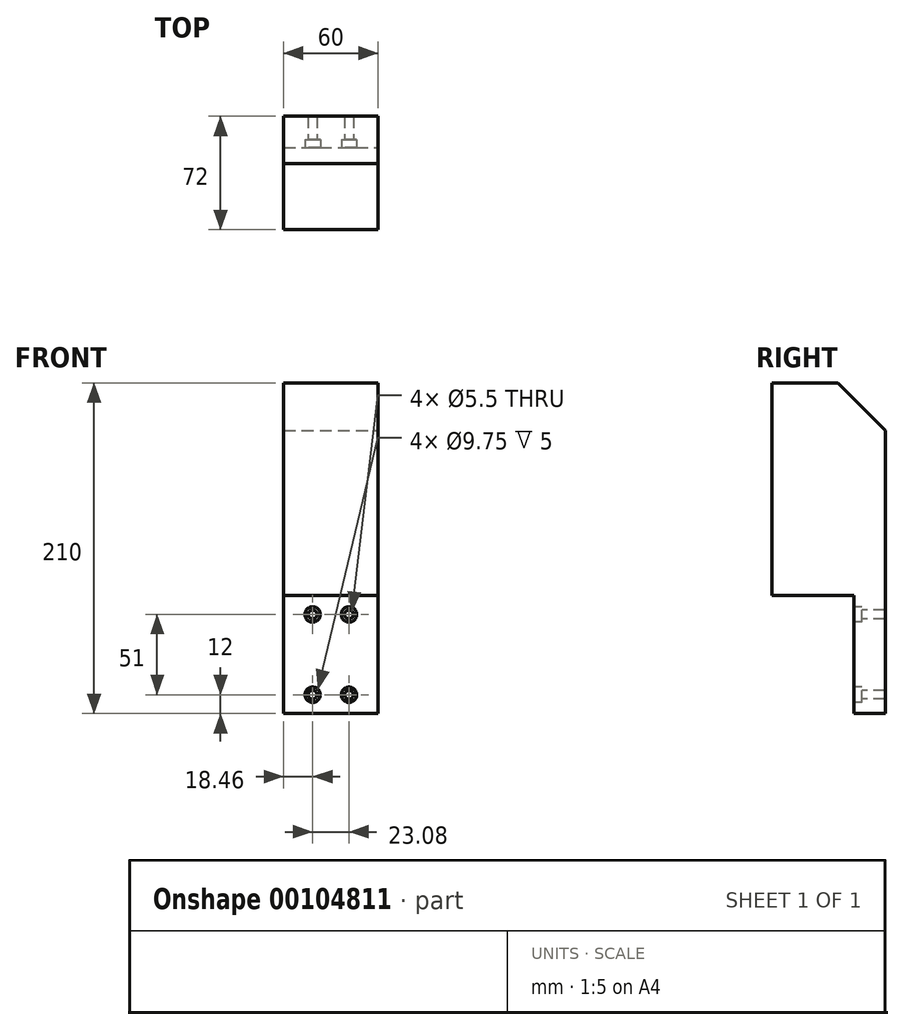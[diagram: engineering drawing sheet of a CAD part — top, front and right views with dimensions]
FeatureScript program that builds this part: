
annotation { "Feature Type Name" : "Feature", "Feature Type Description" : "" }
export const myFeature = defineFeature(function(context is Context, id is Id, definition is map)
    precondition{}
    {
        {
            var Q0;
            Q0=qCreatedBy(makeId("Front.planeOp"),FACE);
            var sketch = newSketch(context, id + "F0", { "sketchPlane" : qUnion([Q0])});
            skLineSegment(sketch, "E0.bottom", {"start": v(-30, 105) * mm, "end": v(30, 105) * mm});
            skLineSegment(sketch, "E0.top", {"start": v(-30, -105) * mm, "end": v(30, -105) * mm});
            skLineSegment(sketch, "E0.left", {"start": v(-30, 105) * mm, "end": v(-30, -105) * mm});
            skLineSegment(sketch, "E0.right", {"start": v(30, 105) * mm, "end": v(30, -105) * mm});
            skPoint(sketch, "E0.middle", {"position": v(0, 0) * mm});
            skSolve(sketch);
        }
        {
            var Q0;
            Q0 = qSketchRegion(id + "F0", true);
            extrude(context, id + "F1", {"entities" : qUnion([Q0]), "depth" : 72 * mm});
        }
        {
            var Q0;
            Q0=makeQuery(id+"F1.opExtrude","SWEPT_FACE",FACE,{"disambiguationData":[OSD([sQuery(id+"F0.wireOp",EDGE,"E0.right")])]});
            var sketch = newSketch(context, id + "F2", { "sketchPlane" : qUnion([Q0])});
            skLineSegment(sketch, "E1.bottom", {"start": v(-72, -105) * mm, "end": v(-20, -105) * mm});
            skLineSegment(sketch, "E1.top", {"start": v(-72, -30) * mm, "end": v(-20, -30) * mm});
            skLineSegment(sketch, "E1.left", {"start": v(-72, -105) * mm, "end": v(-72, -30) * mm});
            skLineSegment(sketch, "E1.right", {"start": v(-20, -105) * mm, "end": v(-20, -30) * mm});
            skSolve(sketch);
        }
        {
            var Q0;
            Q0 = qSketchRegion(id + "F2", true);
            extrude(context, id + "F3", {"entities" : qUnion([Q0]), "operationType" : NewBodyOperationType.REMOVE, "endBound" : BoundingType.THROUGH_ALL, "oppositeDirection" : true, "depth" : 25.4 * mm});
        }
        {
            var Q0;
            Q0=makeQuery(id+"F1.opExtrude","CAP_EDGE",EDGE,{"disambiguationData":[OSD([sQuery(id+"F0.wireOp",EDGE,"E0.bottom")])],"isStart":true});
            chamfer(context, id + "F4", {"entities" : qUnion([Q0]), "width" : 30 * mm, "tangentPropagation" : true});
        }
        {
            var Q0;
            Q0=makeQuery(id+"F3.boolean.opBoolean","COPY",FACE,{"derivedFrom":makeQuery(id+"F3.opExtrude","SWEPT_FACE",FACE,{"disambiguationData":[OSD([sQuery(id+"F2.wireOp",EDGE,"E1.right")])]})});
            cPlane(context, id + "F5", {"entities" : qUnion([Q0]), "cplaneType" : CPlaneType.OFFSET, "offset" : 0 * mm, "width" : 152.4 * mm, "height" : 152.4 * mm});
        }
        {
            var Q0;
            Q0=qCreatedBy(id+"F5.planeOp",FACE);
            var sketch = newSketch(context, id + "F6", { "sketchPlane" : qUnion([Q0])});
            skPoint(sketch, "E2", {"position": v(-11.54, -42) * mm});
            skPoint(sketch, "E3", {"position": v(11.54, -42) * mm});
            skPoint(sketch, "E4", {"position": v(-11.54, -93) * mm});
            skPoint(sketch, "E5", {"position": v(11.54, -93) * mm});
            skLineSegment(sketch, "E6", {"start": v(0, -19.47) * mm, "end": v(0, -135.95) * mm});
            skSolve(sketch);
        }
        {
            var Q0;
            Q0=sQuery(id+"F6.wireOp",VERTEX,"E2");
            var Q1;
            Q1=sQuery(id+"F6.wireOp",VERTEX,"E3");
            var Q2;
            Q2=sQuery(id+"F6.wireOp",VERTEX,"E4");
            var Q3;
            Q3=sQuery(id+"F6.wireOp",VERTEX,"E5");
            var Q4;
            Q4=makeQuery(id+"F1.opExtrude","SWEPT_BODY",BODY,{"disambiguationData":[OSD([sQuery(id+"F0.wireOp",EDGE,"E0.bottom"),sQuery(id+"F0.wireOp",EDGE,"E0.top"),sQuery(id+"F0.wireOp",EDGE,"E0.left"),sQuery(id+"F0.wireOp",EDGE,"E0.right")])]});
            hole(context, id + "F7", {"style" : HoleStyle.C_BORE, "endStyle" : HoleEndStyle.THROUGH, "standardTappedOrClearance" : lookupTablePath({ "standard" : "ISO", "fit" : "Normal", "size" : "M5", "type" : "Clearance" }), "standardBlindInLast" : lookupTablePath({ "fit" : "Standard", "standard" : "ISO", "size" : "M5", "type" : "Clearance" }), "holeDiameter" : 5.5 * mm, "cBoreDiameter" : 9.75 * mm, "cBoreDepth" : 5 * mm, "locations" : qUnion([Q0, Q1, Q2, Q3]), "scope" : qUnion([Q4]), "isTappedThrough" : true});
        }
    });
